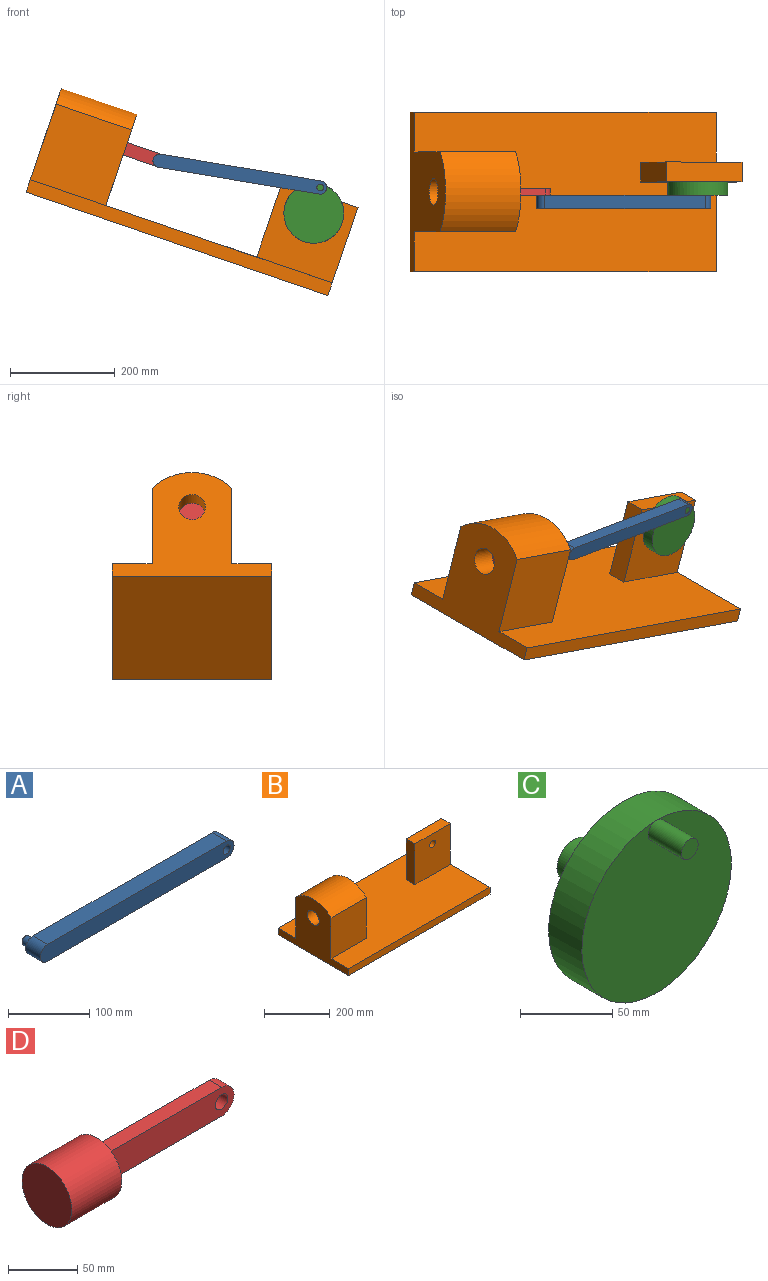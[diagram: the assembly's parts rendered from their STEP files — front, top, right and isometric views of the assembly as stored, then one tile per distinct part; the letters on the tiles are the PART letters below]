
ASSEMBLY  parts=4 mates=4
PART A: 9 faces, bbox 336.6x38.1x25.4 mm
  f0: plane 311.15x25.4mm, normal (0,0,-1), area 7903.2mm2, adj f2,f3,f4,f5
  f1: plane 311.15x25.4mm, normal (0,0,1), area 7903.2mm2, adj f2,f3,f4,f5
  f2: plane 336.55x25.4mm, normal (0,-1,0), area 8283.2mm2, adj f0,f1,f4,f5,f8
  f3: plane 336.55x25.4mm, normal (0,1,0), area 8156.6mm2, adj f0,f1,f4,f5,f6,f8
  f4: cylinder r=12.7mm len=25.4mm, axis (0,-1,0), area 1013.4mm2, adj f0,f1,f2,f3
  f5: cylinder r=12.7mm len=25.4mm, axis (0,1,0), area 1013.4mm2, adj f0,f1,f2,f3
  f6: cylinder r=6.35mm len=12.7mm, axis (0,-1,0), area 506.7mm2, adj f3,f7
  f7: plane 12.7x12.7mm, normal (0,1,0), area 126.7mm2, adj f6
  f8: cylinder r=6.35mm len=25.4mm, axis (0,1,0), area 1013.4mm2, adj f2,f3
PART B: 16 faces, bbox 609.6x304.8x209.7 mm
  f0: plane 609.6x304.8mm, normal (0,0,1), area 156773.9mm2, adj f1,f2,f3,f4,f6,f7,f8,f10
  f1: plane 304.8x209.66mm, normal (-1,0,0), area 32288.4mm2, adj f0,f2,f4,f5,f6,f8,f9,f15
  f2: plane 609.6x25.4mm, normal (0,-1,0), area 15483.8mm2, adj f0,f1,f3,f5
  f3: plane 304.8x177.8mm, normal (1,0,0), area 13548.4mm2, adj f0,f2,f4,f5,f10,f11,f13
  f4: plane 609.6x25.4mm, normal (0,1,0), area 15483.8mm2, adj f0,f1,f3,f5
  f5: plane 609.6x304.8mm, normal (0,0,-1), area 185806.1mm2, adj f1,f2,f3,f4
  f6: plane 152.4x152.4mm, normal (0,-1,0), area 23225.8mm2, adj f0,f1,f7,f15
  f7: plane 184.26x152.4mm, normal (1,0,0), area 24546.4mm2, adj f0,f6,f8,f9,f15
  f8: plane 152.4x152.4mm, normal (0,1,0), area 23225.8mm2, adj f0,f1,f7,f15
  f9: cylinder r=25.4mm len=152.4mm, axis (1,0,0), area 24322mm2, adj f1,f7
  f10: plane 152.4x152.4mm, normal (0,-1,0), area 22719.1mm2, adj f0,f3,f12,f13,f14
  f11: plane 152.4x152.4mm, normal (0,1,0), area 22719.1mm2, adj f0,f3,f12,f13,f14
  f12: plane 152.4x38.1mm, normal (-1,0,0), area 5806.4mm2, adj f0,f10,f11,f13
  f13: plane 152.4x38.1mm, normal (0,0,1), area 5806.4mm2, adj f3,f10,f11,f12
  f14: cylinder r=12.7mm len=38.1mm, axis (0,-1,0), area 3040.2mm2, adj f10,f11
  f15: cylinder r=107.05mm len=152.4mm, axis (1,0,0), area 25844.5mm2, adj f1,f6,f7,f8
PART C: 7 faces, bbox 114.3x88.9x114.3 mm
  f0: cylinder r=57.15mm len=114.3mm, axis (0,1,0), area 9120.7mm2, adj f1,f2
  f1: plane 114.3x114.3mm, normal (0,-1,0), area 10134.1mm2, adj f0,f5
  f2: plane 114.3x114.3mm, normal (0,1,0), area 9754.1mm2, adj f0,f3
  f3: cylinder r=12.7mm len=38.1mm, axis (0,-1,0), area 3040.2mm2, adj f2,f4
  f4: plane 25.4x25.4mm, normal (0,1,0), area 506.7mm2, adj f3
  f5: cylinder r=6.35mm len=25.4mm, axis (0,1,0), area 1013.4mm2, adj f1,f6
  f6: plane 12.7x12.7mm, normal (0,-1,0), area 126.7mm2, adj f5
PART D: 9 faces, bbox 184.2x50.8x50.8 mm
  f0: cylinder r=25.4mm len=50.8mm, axis (1,0,0), area 8107.3mm2, adj f1,f2
  f1: plane 50.8x50.8mm, normal (-1,0,0), area 2026.8mm2, adj f0
  f2: plane 50.8x50.8mm, normal (1,0,0), area 1704.2mm2, adj f0,f3,f4,f5,f6
  f3: plane 133.35x25.4mm, normal (0,-1,0), area 3191.2mm2, adj f2,f4,f6,f7,f8
  f4: plane 120.65x12.7mm, normal (0,0,-1), area 1532.3mm2, adj f2,f3,f5,f7
  f5: plane 133.35x25.4mm, normal (0,1,0), area 3191.2mm2, adj f2,f4,f6,f7,f8
  f6: plane 120.65x12.7mm, normal (0,0,1), area 1532.3mm2, adj f2,f3,f5,f7
  f7: cylinder r=12.7mm len=25.4mm, axis (0,1,0), area 506.7mm2, adj f3,f4,f5,f6
  f8: cylinder r=6.35mm len=12.7mm, axis (0,-1,0), area 506.7mm2, adj f3,f5
PLACE A rot(axis=(0,1,0),9.5deg) t=(-57.12,12.74,200.07)mm
PLACE B rot(axis=(0,1,0),18.9deg) t=(-142.91,19.09,69.38)mm fixed
PLACE C rot(axis=(0,1,0),13.9deg) t=(110.37,38.14,103.59)mm
PLACE D rot(axis=(0,1,0),18.9deg) t=(-298.44,19.09,243.34)mm
MATE revolute A.f4 <-> D.f7  axis (0,-1,0) through (-184.28,19.09,204.31)mm
MATE slider D.f0 <-> B.f9  axis (0.95,0,-0.32) through (-322.48,19.09,251.55)mm
MATE revolute C.f0 <-> B.f14  axis (0,1,0) through (110.37,76.24,103.59)mm
MATE revolute A.f5 <-> C.f5  axis (0,1,0) through (122.59,0.04,152.9)mm
